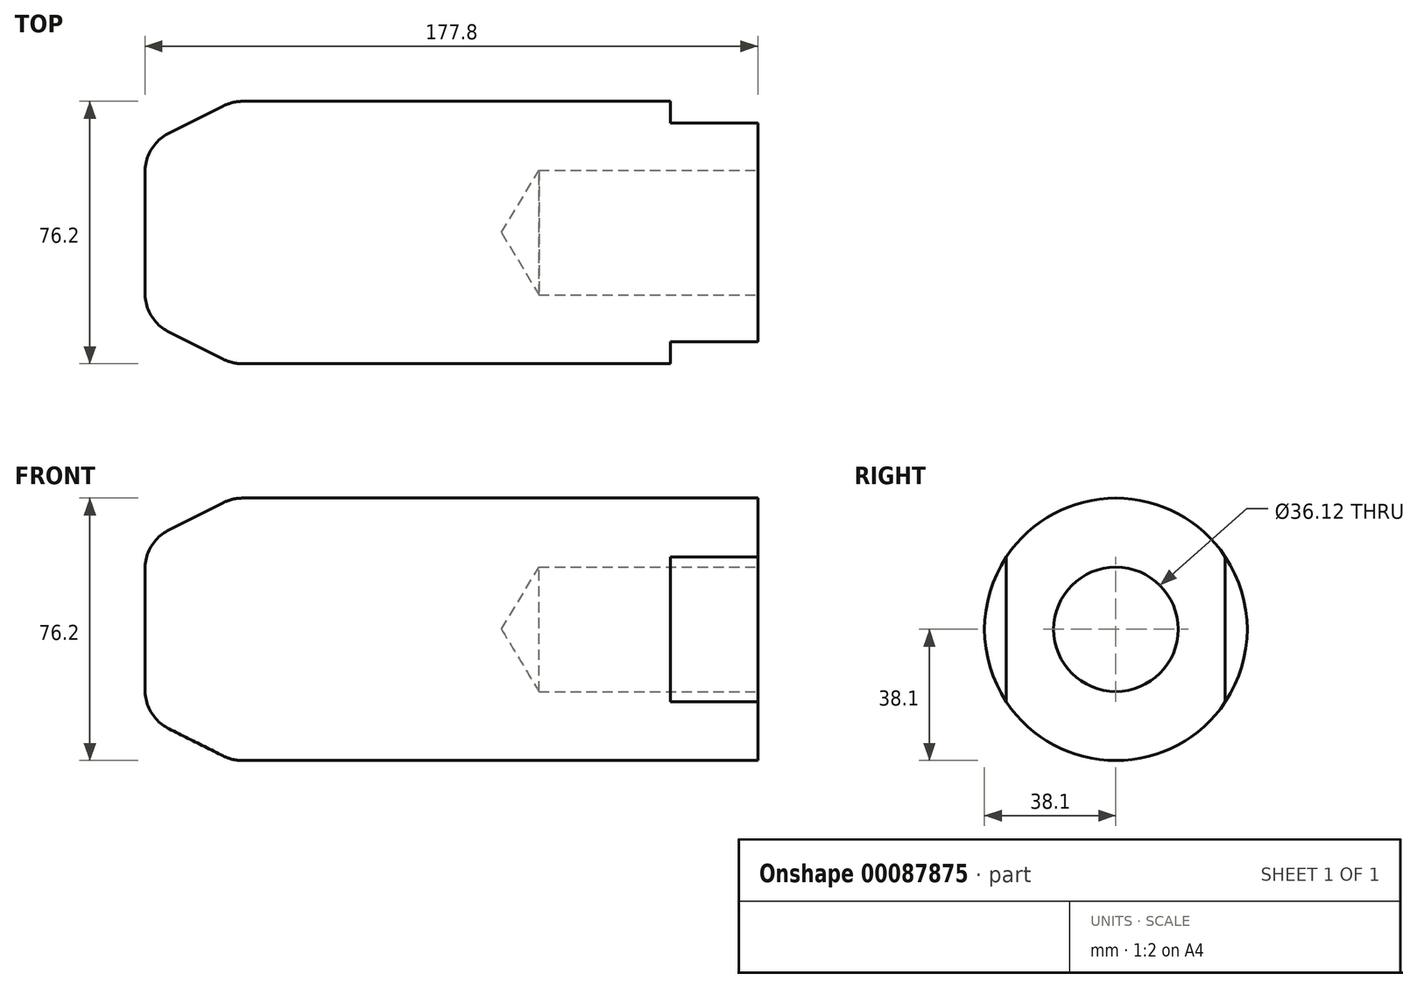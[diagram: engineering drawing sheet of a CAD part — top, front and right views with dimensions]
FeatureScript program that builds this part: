
annotation { "Feature Type Name" : "Feature", "Feature Type Description" : "" }
export const myFeature = defineFeature(function(context is Context, id is Id, definition is map)
    precondition{}
    {
        {
            var Q0;
            Q0=qCreatedBy(makeId("Right.planeOp"),FACE);
            var sketch = newSketch(context, id + "F0", { "sketchPlane" : qUnion([Q0])});
            skCircle(sketch, "E0", {"center": v(0, 0) * mm, "radius": 38.1 * mm});
            skSolve(sketch);
        }
        {
            var Q0;
            Q0 = qSketchRegion(id + "F0", true);
            extrude(context, id + "F1", {"entities" : qUnion([Q0]), "oppositeDirection" : true, "depth" : 177.8 * mm});
        }
        {
            var Q0;
            Q0=makeQuery(id+"F1.opExtrude","CAP_FACE",FACE,{"disambiguationData":[OSD([sQuery(id+"F0.wireOp",EDGE,"E0")])],"isStart":true});
            var sketch = newSketch(context, id + "F2", { "sketchPlane" : qUnion([Q0])});
            skPoint(sketch, "E1", {"position": v(0, 0) * mm});
            skSolve(sketch);
        }
        {
            var Q0;
            Q0=makeQuery(id+"F2.imprint","IMPRINT",FACE,{"disambiguationData":[TD([[makeQuery(id+"F2.imprint","IMPRINT",EDGE,{"derivedFrom":makeQuery(id+"F1.opExtrude","CAP_EDGE",EDGE,{"disambiguationData":[OSD([sQuery(id+"F0.wireOp",EDGE,"E0")])],"isStart":true})}),1.0]])]});
            var sketch = newSketch(context, id + "F3", { "sketchPlane" : qUnion([Q0])});
            skPoint(sketch, "E2", {"position": v(0, 0) * mm});
            skSolve(sketch);
        }
        {
            var Q0;
            Q0=sQuery(id+"F3.wireOp",VERTEX,"E2");
            var Q1;
            Q1=makeQuery(id+"F1.opExtrude","SWEPT_BODY",BODY,{"disambiguationData":[OSD([sQuery(id+"F0.wireOp",EDGE,"E0")])]});
            hole(context, id + "F4", {"style" : HoleStyle.SIMPLE, "endStyle" : HoleEndStyle.BLIND, "standardTappedOrClearance" : lookupTablePath({ "standard" : "ANSI", "engagement" : "75%", "pitch" : "12 tpi", "size" : "1 1/2", "type" : "Tapped" }), "standardBlindInLast" : lookupTablePath({ "standard" : "ANSI", "engagement" : "75%", "pitch" : "12 tpi", "size" : "1 1/2", "type" : "Tapped" }), "holeDiameter" : 36.12 * mm, "holeDepth" : 63.5 * mm, "locations" : qUnion([Q0]), "scope" : qUnion([Q1]), "majorDiameter" : 38.1 * mm});
        }
        {
            var Q0;
            Q0=makeQuery(id+"F1.opExtrude","CAP_EDGE",EDGE,{"disambiguationData":[OSD([sQuery(id+"F0.wireOp",EDGE,"E0")])],"isStart":false});
            chamfer(context, id + "F5", {"entities" : qUnion([Q0]), "chamferType" : ChamferType.TWO_OFFSETS, "width1" : 25.4 * mm, "oppositeDirection" : false, "width2" : 12.7 * mm, "tangentPropagation" : true});
        }
        {
            var Q0;
            {var subQ0=sQuery(id+"F0.wireOp",EDGE,"E0");Q0=makeQuery(id+"F5.opChamfer","BLEND_EDGE",EDGE,{"blendedFrom":[makeQuery(id+"F1.opExtrude","CAP_EDGE",EDGE,{"disambiguationData":[OSD([subQ0])],"isStart":false}),makeQuery(id+"F1.opExtrude","CAP_FACE",FACE,{"disambiguationData":[OSD([subQ0])],"isStart":false})],"blendedInto":[makeQuery(id+"F1.opExtrude","CAP_FACE",FACE,{"disambiguationData":[OSD([subQ0])],"isStart":false})]});}
            var Q1;
            {var subQ0=sQuery(id+"F0.wireOp",EDGE,"E0");Q1=makeQuery(id+"F5.opChamfer","BLEND_EDGE",EDGE,{"blendedFrom":[makeQuery(id+"F1.opExtrude","CAP_EDGE",EDGE,{"disambiguationData":[OSD([subQ0])],"isStart":false}),makeQuery(id+"F1.opExtrude","SWEPT_FACE",FACE,{"disambiguationData":[OSD([subQ0])]})],"blendedInto":[makeQuery(id+"F1.opExtrude","SWEPT_FACE",FACE,{"disambiguationData":[OSD([subQ0])]})]});}
            fillet(context, id + "F6", {"entities" : qUnion([Q0, Q1]), "radius" : 12.7 * mm, "tangentPropagation" : true, "allowEdgeOverflow" : false});
        }
        {
            var Q0;
            Q0=qCreatedBy(makeId("Top.planeOp"),FACE);
            var sketch = newSketch(context, id + "F7", { "sketchPlane" : qUnion([Q0])});
            skLineSegment(sketch, "E3", {"start": v(16.98, 0) * mm, "end": v(-205.61, 0) * mm, "construction": true});
            skLineSegment(sketch, "E4", {"start": v(0, -38.1) * mm, "end": v(-149.4, -38.1) * mm, "construction": true});
            skLineSegment(sketch, "E5", {"start": v(-149.4, 38.1) * mm, "end": v(0, 38.1) * mm, "construction": true});
            skLineSegment(sketch, "E6.0", {"start": v(-149.4, 31.75) * mm, "end": v(0, 31.75) * mm, "construction": true});
            skLineSegment(sketch, "E7.bottom", {"start": v(0, 31.75) * mm, "end": v(-25.4, 31.75) * mm});
            skLineSegment(sketch, "E7.top", {"start": v(0, 38.1) * mm, "end": v(-25.4, 38.1) * mm});
            skLineSegment(sketch, "E7.left", {"start": v(0, 31.75) * mm, "end": v(0, 38.1) * mm});
            skLineSegment(sketch, "E7.right", {"start": v(-25.4, 31.75) * mm, "end": v(-25.4, 38.1) * mm});
            skLineSegment(sketch, "E8.MirrorCS", {"start": v(-25.4, -31.75) * mm, "end": v(-25.4, -38.1) * mm});
            skLineSegment(sketch, "E9.MirrorCS", {"start": v(0, -31.75) * mm, "end": v(0, -38.1) * mm});
            skLineSegment(sketch, "E10.MirrorCS", {"start": v(0, -38.1) * mm, "end": v(-25.4, -38.1) * mm});
            skLineSegment(sketch, "E11.MirrorCS", {"start": v(0, -31.75) * mm, "end": v(-25.4, -31.75) * mm});
            skSolve(sketch);
        }
        {
            var Q0;
            Q0 = qSketchRegion(id + "F7", true);
            extrude(context, id + "F8", {"entities" : qUnion([Q0]), "operationType" : NewBodyOperationType.REMOVE, "endBound" : BoundingType.SYMMETRIC, "oppositeDirection" : true, "depth" : 101.6 * mm});
        }
    });
